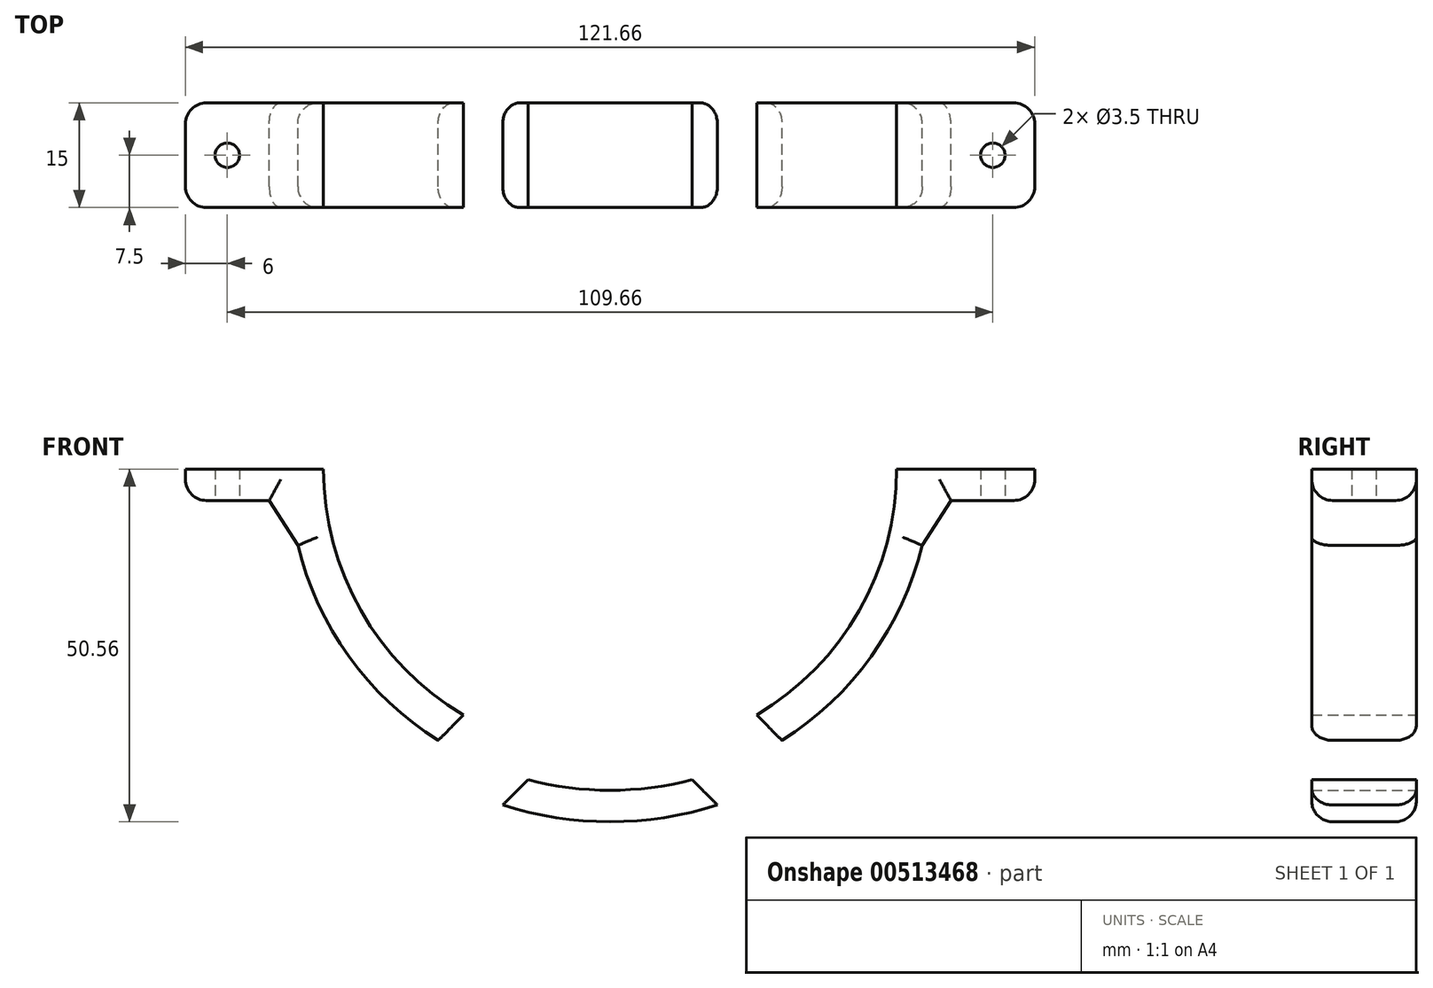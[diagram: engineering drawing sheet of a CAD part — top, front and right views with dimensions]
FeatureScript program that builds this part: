
annotation { "Feature Type Name" : "Feature", "Feature Type Description" : "" }
export const myFeature = defineFeature(function(context is Context, id is Id, definition is map)
    precondition{}
    {
        {
            var Q0;
            Q0=qCreatedBy(makeId("Front.planeOp"),FACE);
            var sketch = newSketch(context, id + "F0", { "sketchPlane" : qUnion([Q0])});
            skArc(sketch, "E0", {"start": v(-41.05, 0) * mm, "mid": v(0, -41.05) * mm, "end": v(41.05, 0) * mm});
            skArc(sketch, "E1", {"start": v(-44.73, -10.94) * mm, "mid": v(-37.4, -26.87) * mm, "end": v(-24.63, -38.9) * mm});
            skLineSegment(sketch, "E2", {"start": v(0, 0) * mm, "end": v(80, 0) * mm, "construction": true});
            skLineSegment(sketch, "E3", {"start": v(-41.05, 0) * mm, "end": v(-60.83, 0) * mm});
            skLineSegment(sketch, "E4", {"start": v(-60.83, 0) * mm, "end": v(-60.83, -4.5) * mm});
            skLineSegment(sketch, "E5", {"start": v(-60.83, -4.5) * mm, "end": v(-48.83, -4.5) * mm});
            skLineSegment(sketch, "E6", {"start": v(-48.83, -4.5) * mm, "end": v(-44.73, -10.94) * mm});
            skLineSegment(sketch, "E7", {"start": v(0, 18.17) * mm, "end": v(0, -51.3) * mm, "construction": true});
            skLineSegment(sketch, "E8", {"start": v(0, -41.05) * mm, "end": v(-21, -41.05) * mm, "construction": true});
            skLineSegment(sketch, "E9", {"start": v(-21, -41.05) * mm, "end": v(-21, -35.27) * mm, "construction": true});
            skLineSegment(sketch, "E10.MirrorCS", {"start": v(0, -41.05) * mm, "end": v(21, -41.05) * mm, "construction": true});
            skLineSegment(sketch, "E11.MirrorCS", {"start": v(21, -41.05) * mm, "end": v(21, -35.27) * mm, "construction": true});
            skLineSegment(sketch, "E12.MirrorCS", {"start": v(41.05, 0) * mm, "end": v(60.83, 0) * mm});
            skLineSegment(sketch, "E13.MirrorCS", {"start": v(60.83, 0) * mm, "end": v(60.83, -4.5) * mm});
            skLineSegment(sketch, "E14.MirrorCS", {"start": v(60.83, -4.5) * mm, "end": v(48.83, -4.5) * mm});
            skLineSegment(sketch, "E15.MirrorCS", {"start": v(48.83, -4.5) * mm, "end": v(44.73, -10.94) * mm});
            skLineSegment(sketch, "E16", {"start": v(-21, -35.27) * mm, "end": v(-24.63, -38.9) * mm});
            skLineSegment(sketch, "E17", {"start": v(-21, -35.27) * mm, "end": v(-11.74, -44.53) * mm});
            skLineSegment(sketch, "E18", {"start": v(-15.38, -48.16) * mm, "end": v(-11.74, -44.53) * mm});
            skLineSegment(sketch, "E19.MirrorCS", {"start": v(24.63, -38.9) * mm, "end": v(15.38, -48.16) * mm});
            skLineSegment(sketch, "E20.MirrorCS", {"start": v(15.38, -48.16) * mm, "end": v(11.74, -44.53) * mm});
            skLineSegment(sketch, "E21.MirrorCS", {"start": v(21, -35.27) * mm, "end": v(11.74, -44.53) * mm});
            skLineSegment(sketch, "E22.MirrorCS", {"start": v(21, -35.27) * mm, "end": v(24.63, -38.9) * mm});
            skLineSegment(sketch, "E23", {"start": v(-24.63, -38.9) * mm, "end": v(-15.38, -48.16) * mm});
            skArc(sketch, "E24", {"start": v(-15.38, -48.16) * mm, "mid": v(0, -50.56) * mm, "end": v(15.38, -48.16) * mm});
            skArc(sketch, "E25.trimOffspring", {"start": v(-11.74, -44.53) * mm, "mid": v(0, -46.05) * mm, "end": v(11.74, -44.53) * mm});
            skArc(sketch, "E26.trimOffspring", {"start": v(20.87, -41.05) * mm, "mid": v(20.93, -41.02) * mm, "end": v(21, -40.98) * mm});
            skArc(sketch, "E27.trimOffspring", {"start": v(24.63, -38.9) * mm, "mid": v(37.4, -26.87) * mm, "end": v(44.73, -10.94) * mm});
            skArc(sketch, "E28.trimOffspring", {"start": v(-21, -40.98) * mm, "mid": v(-20.93, -41.02) * mm, "end": v(-20.87, -41.05) * mm});
            skLineSegment(sketch, "E29", {"start": v(0, 0) * mm, "end": v(-100.13, 0) * mm, "construction": true});
            skSolve(sketch);
        }
        {
            var Q0;
            Q0=makeQuery(id+"F0.imprint","IMPRINT",FACE,{"disambiguationData":[TD([[makeQuery(id+"F0.imprint","IMPRINT",EDGE,{"derivedFrom":sQuery(id+"F0.wireOp",EDGE,"E1")}),1.0]])]});
            var Q1;
            {var subQ0=sQuery(id+"F0.wireOp",EDGE,"E15.MirrorCS");Q1=makeQuery(id+"F0.imprint","IMPRINT",FACE,{"disambiguationData":[TD([[makeQuery(id+"F0.imprint","IMPRINT",EDGE,{"derivedFrom":subQ0}),-1.0]])]});}
            var Q2;
            {var subQ0=sQuery(id+"F0.wireOp",EDGE,"E13.MirrorCS");Q2=makeQuery(id+"F0.imprint","IMPRINT",FACE,{"disambiguationData":[TD([[makeQuery(id+"F0.imprint","IMPRINT",EDGE,{"derivedFrom":subQ0}),-1.0]])]});}
            var Q3;
            {var subQ0=sQuery(id+"F0.wireOp",EDGE,"E4");Q3=makeQuery(id+"F0.imprint","IMPRINT",FACE,{"disambiguationData":[TD([[makeQuery(id+"F0.imprint","IMPRINT",EDGE,{"derivedFrom":subQ0}),1.0]])]});}
            var Q4;
            Q4=makeQuery(id+"F0.imprint","IMPRINT",FACE,{"disambiguationData":[TD([[makeQuery(id+"F0.imprint","IMPRINT",EDGE,{"derivedFrom":sQuery(id+"F0.wireOp",EDGE,"E18")}),-1.0]])]});
            var Q5;
            Q5=makeQuery(id+"F0.imprint","IMPRINT",FACE,{"disambiguationData":[TD([[makeQuery(id+"F0.imprint","IMPRINT",EDGE,{"derivedFrom":sQuery(id+"F0.wireOp",EDGE,"E16")}),1.0]])]});
            var Q6;
            Q6=makeQuery(id+"F0.imprint","IMPRINT",FACE,{"disambiguationData":[TD([[makeQuery(id+"F0.imprint","IMPRINT",EDGE,{"derivedFrom":sQuery(id+"F0.wireOp",EDGE,"E22.MirrorCS")}),-1.0]])]});
            extrude(context, id + "F1", {"entities" : qUnion([Q0, Q1, Q2, Q3, Q4, Q5, Q6]), "depth" : 15 * mm, "offsetDistance" : 25 * mm});
        }
        {
            var Q0;
            Q0=makeQuery(id+"F1.opExtrude","SWEPT_FACE",FACE,{"disambiguationData":[OSD([sQuery(id+"F0.wireOp",EDGE,"E5")])]});
            var sketch = newSketch(context, id + "F2", { "sketchPlane" : qUnion([Q0])});
            skLineSegment(sketch, "E30.0", {"start": v(-54.83, 15) * mm, "end": v(-54.83, 0) * mm});
            skLineSegment(sketch, "E31.0", {"start": v(-60.83, 7.5) * mm, "end": v(-48.83, 7.5) * mm});
            skCircle(sketch, "E32", {"center": v(-54.83, 7.5) * mm, "radius": 1.75 * mm});
            skSolve(sketch);
        }
        {
            var Q0;
            Q0=makeQuery(id+"F1.opExtrude","SWEPT_FACE",FACE,{"disambiguationData":[OSD([sQuery(id+"F0.wireOp",EDGE,"E14.MirrorCS")])]});
            var sketch = newSketch(context, id + "F3", { "sketchPlane" : qUnion([Q0])});
            skLineSegment(sketch, "E33.0", {"start": v(54.83, 15) * mm, "end": v(54.83, 0) * mm});
            skLineSegment(sketch, "E34.0", {"start": v(60.83, 7.5) * mm, "end": v(48.83, 7.5) * mm});
            skCircle(sketch, "E35", {"center": v(54.83, 7.5) * mm, "radius": 1.75 * mm});
            skSolve(sketch);
        }
        {
            var Q0;
            Q0=sQuery(id+"F2.wireOp",VERTEX,"E32.center");
            var Q1;
            Q1=sQuery(id+"F3.wireOp",VERTEX,"E35.center");
            var Q2;
            Q2=makeQuery(id+"F1.opExtrude","SWEPT_BODY",BODY,{"disambiguationData":[OSD([sQuery(id+"F0.wireOp",EDGE,"E0"),sQuery(id+"F0.wireOp",EDGE,"E1"),sQuery(id+"F0.wireOp",EDGE,"E3"),sQuery(id+"F0.wireOp",EDGE,"E4"),sQuery(id+"F0.wireOp",EDGE,"E5"),sQuery(id+"F0.wireOp",EDGE,"E6"),sQuery(id+"F0.wireOp",EDGE,"E12.MirrorCS"),sQuery(id+"F0.wireOp",EDGE,"E13.MirrorCS"),sQuery(id+"F0.wireOp",EDGE,"E14.MirrorCS"),sQuery(id+"F0.wireOp",EDGE,"E15.MirrorCS"),sQuery(id+"F0.wireOp",EDGE,"E17"),sQuery(id+"F0.wireOp",EDGE,"E23"),sQuery(id+"F0.wireOp",EDGE,"E24"),sQuery(id+"F0.wireOp",EDGE,"E19.MirrorCS"),sQuery(id+"F0.wireOp",EDGE,"E21.MirrorCS"),sQuery(id+"F0.wireOp",EDGE,"E25.trimOffspring"),sQuery(id+"F0.wireOp",EDGE,"E27.trimOffspring")])]});
            hole(context, id + "F4", {"style" : HoleStyle.SIMPLE, "endStyle" : HoleEndStyle.BLIND, "holeDiameter" : 3.5 * mm, "holeDepth" : 14.5 * mm, "isTappedThrough" : true, "tappedDepth" : 12 * mm, "tapClearance" : 3, "locations" : qUnion([Q0, Q1]), "scope" : qUnion([Q2])});
        }
        {
            var Q0;
            Q0=makeQuery(id+"F1.opExtrude","CAP_EDGE",EDGE,{"disambiguationData":[OSD([sQuery(id+"F0.wireOp",EDGE,"E4")])],"isStart":true});
            var Q1;
            Q1=makeQuery(id+"F1.opExtrude","CAP_EDGE",EDGE,{"disambiguationData":[OSD([sQuery(id+"F0.wireOp",EDGE,"E5")])],"isStart":true});
            var Q2;
            Q2=makeQuery(id+"F1.opExtrude","SWEPT_EDGE",EDGE,{"disambiguationData":[OSD([sQuery(id+"F0.wireOp",EDGE,"E4"),sQuery(id+"F0.wireOp",EDGE,"E5")])]});
            var Q3;
            Q3=makeQuery(id+"F1.opExtrude","CAP_EDGE",EDGE,{"disambiguationData":[OSD([sQuery(id+"F0.wireOp",EDGE,"E4")])],"isStart":false});
            var Q4;
            Q4=makeQuery(id+"F1.opExtrude","CAP_EDGE",EDGE,{"disambiguationData":[OSD([sQuery(id+"F0.wireOp",EDGE,"E5")])],"isStart":false});
            var Q5;
            Q5=makeQuery(id+"F1.opExtrude","CAP_EDGE",EDGE,{"disambiguationData":[OSD([sQuery(id+"F0.wireOp",EDGE,"E6")])],"isStart":false});
            var Q6;
            Q6=makeQuery(id+"F1.opExtrude","CAP_EDGE",EDGE,{"disambiguationData":[OSD([sQuery(id+"F0.wireOp",EDGE,"E6")])],"isStart":true});
            var Q7;
            Q7=makeQuery(id+"F1.opExtrude","CAP_EDGE",EDGE,{"disambiguationData":[OSD([sQuery(id+"F0.wireOp",EDGE,"E23")])],"isStart":true});
            var Q8;
            Q8=makeQuery(id+"F1.opExtrude","CAP_EDGE",EDGE,{"disambiguationData":[OSD([sQuery(id+"F0.wireOp",EDGE,"E1")])],"isStart":true});
            var Q9;
            Q9=makeQuery(id+"F1.opExtrude","CAP_EDGE",EDGE,{"disambiguationData":[OSD([sQuery(id+"F0.wireOp",EDGE,"E24")])],"isStart":true});
            var Q10;
            Q10=makeQuery(id+"F1.opExtrude","CAP_EDGE",EDGE,{"disambiguationData":[OSD([sQuery(id+"F0.wireOp",EDGE,"E19.MirrorCS")])],"isStart":true});
            var Q11;
            Q11=makeQuery(id+"F1.opExtrude","CAP_EDGE",EDGE,{"disambiguationData":[OSD([sQuery(id+"F0.wireOp",EDGE,"E27.trimOffspring")])],"isStart":true});
            var Q12;
            Q12=makeQuery(id+"F1.opExtrude","CAP_EDGE",EDGE,{"disambiguationData":[OSD([sQuery(id+"F0.wireOp",EDGE,"E15.MirrorCS")])],"isStart":true});
            var Q13;
            Q13=makeQuery(id+"F1.opExtrude","CAP_EDGE",EDGE,{"disambiguationData":[OSD([sQuery(id+"F0.wireOp",EDGE,"E14.MirrorCS")])],"isStart":true});
            var Q14;
            Q14=makeQuery(id+"F1.opExtrude","SWEPT_EDGE",EDGE,{"disambiguationData":[OSD([sQuery(id+"F0.wireOp",EDGE,"E13.MirrorCS"),sQuery(id+"F0.wireOp",EDGE,"E14.MirrorCS")])]});
            var Q15;
            Q15=makeQuery(id+"F1.opExtrude","CAP_EDGE",EDGE,{"disambiguationData":[OSD([sQuery(id+"F0.wireOp",EDGE,"E13.MirrorCS")])],"isStart":false});
            var Q16;
            Q16=makeQuery(id+"F1.opExtrude","CAP_EDGE",EDGE,{"disambiguationData":[OSD([sQuery(id+"F0.wireOp",EDGE,"E14.MirrorCS")])],"isStart":false});
            var Q17;
            Q17=makeQuery(id+"F1.opExtrude","CAP_EDGE",EDGE,{"disambiguationData":[OSD([sQuery(id+"F0.wireOp",EDGE,"E15.MirrorCS")])],"isStart":false});
            var Q18;
            Q18=makeQuery(id+"F1.opExtrude","CAP_EDGE",EDGE,{"disambiguationData":[OSD([sQuery(id+"F0.wireOp",EDGE,"E23")])],"isStart":false});
            var Q19;
            Q19=makeQuery(id+"F1.opExtrude","CAP_EDGE",EDGE,{"disambiguationData":[OSD([sQuery(id+"F0.wireOp",EDGE,"E24")])],"isStart":false});
            var Q20;
            Q20=makeQuery(id+"F1.opExtrude","CAP_EDGE",EDGE,{"disambiguationData":[OSD([sQuery(id+"F0.wireOp",EDGE,"E19.MirrorCS")])],"isStart":false});
            var Q21;
            Q21=makeQuery(id+"F1.opExtrude","CAP_EDGE",EDGE,{"disambiguationData":[OSD([sQuery(id+"F0.wireOp",EDGE,"E27.trimOffspring")])],"isStart":false});
            var Q22;
            Q22=makeQuery(id+"F1.opExtrude","CAP_EDGE",EDGE,{"disambiguationData":[OSD([sQuery(id+"F0.wireOp",EDGE,"E1")])],"isStart":false});
            var Q23;
            Q23=makeQuery(id+"F1.opExtrude","CAP_EDGE",EDGE,{"disambiguationData":[OSD([sQuery(id+"F0.wireOp",EDGE,"E13.MirrorCS")])],"isStart":true});
            fillet(context, id + "F5", {"entities" : qUnion([Q0, Q1, Q2, Q3, Q4, Q5, Q6, Q7, Q8, Q9, Q10, Q11, Q12, Q13, Q14, Q15, Q16, Q17, Q18, Q19, Q20, Q21, Q22, Q23]), "radius" : 3 * mm, "tangentPropagation" : true, "allowEdgeOverflow" : false});
        }
    });
